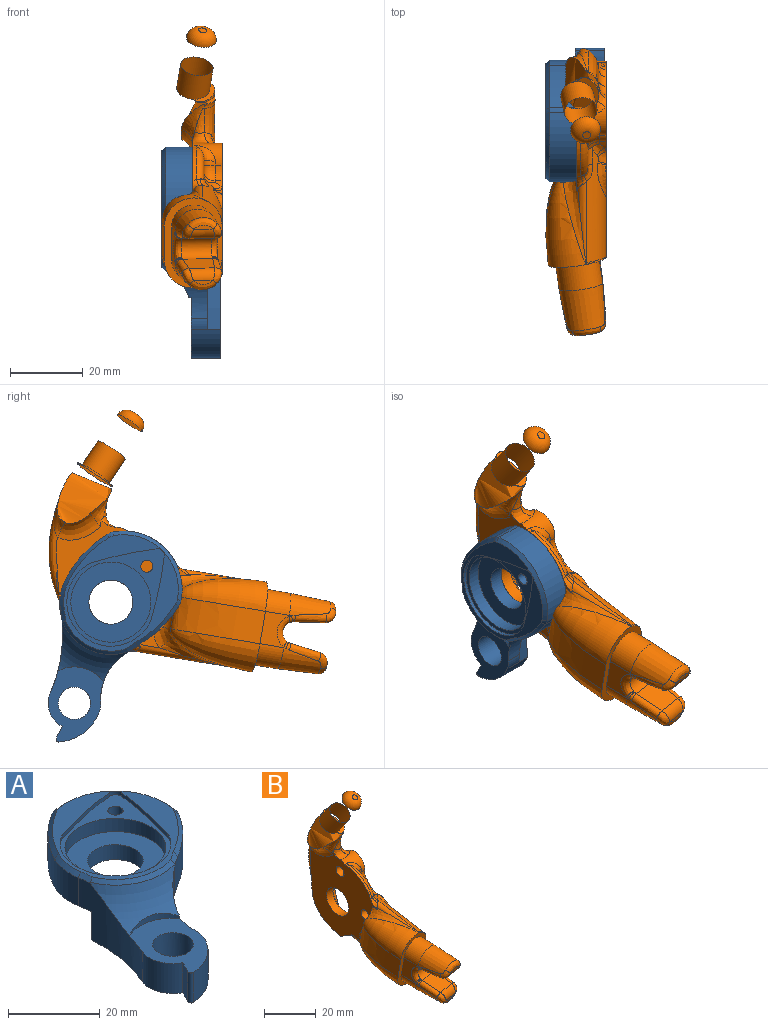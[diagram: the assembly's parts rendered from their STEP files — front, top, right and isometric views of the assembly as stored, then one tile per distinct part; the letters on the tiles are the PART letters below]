
ASSEMBLY  parts=2 mates=1
PART A: 46 faces, bbox 45.5x58x20.8 mm
  f0: cylinder r=15mm len=13.08mm, axis (0,0,-1), area 89.6mm2, adj f3,f6,f18,f19,f21,f31,f42,f44
  f1: cylinder r=40mm len=22.59mm, axis (0,0,-1), area 218.8mm2, adj f3,f6,f7,f11,f12,f21,f31,f40
  f2: cylinder r=4.45mm len=8.9mm, axis (0,0,-1), area 223.7mm2, adj f7,f31
  f3: torus R=25.75mm, axis (0,0,-1), area 148.1mm2, adj f0,f1,f18,f34,f40,f42,f43
  f4: cylinder r=6.06mm len=12.13mm, axis (0,0,-1), area 152.4mm2, adj f6,f33
  f5: cylinder r=1.65mm len=7.5mm, axis (0,0,-1), area 77.8mm2, adj f6,f30
  f6: plane 35.24x33.45mm, normal (0,0,-1), area 708.6mm2, adj f0,f1,f4,f5,f12,f13,f14,f15
  f7: plane 32.44x13.88mm, normal (0,0,-1), area 216.4mm2, adj f1,f2,f8,f9,f10,f11,f19,f21
  f8: cylinder r=12.7mm len=10.93mm, axis (0,0,-1), area 113.9mm2, adj f7,f9,f19,f31
  f9: cylinder r=0.75mm len=8mm, axis (0,0,-1), area 12.7mm2, adj f7,f8,f10,f31
  f10: plane 8x3.14mm, normal (-0.89,0.46,0), area 28.3mm2, adj f7,f9,f11,f31
  f11: cylinder r=7.2mm len=9.28mm, axis (0,0,-1), area 86.6mm2, adj f1,f7,f10,f31
  f12: cylinder r=13.95mm len=8.84mm, axis (0,0,-1), area 68.4mm2, adj f1,f6,f13,f41
  f13: cylinder r=31.7mm len=12.1mm, axis (0,0,-1), area 126.2mm2, adj f6,f12,f14,f39
  f14: cylinder r=4.26mm len=7.5mm, axis (0,0,-1), area 11.6mm2, adj f6,f13,f15,f38
  f15: cylinder r=16mm len=18.98mm, axis (0,0,-1), area 233.5mm2, adj f6,f14,f16,f37
  f16: cylinder r=4.26mm len=7.5mm, axis (0,0,-1), area 11.6mm2, adj f6,f15,f17,f36
  f17: cylinder r=31.7mm len=11.35mm, axis (0,0,-1), area 119.7mm2, adj f6,f16,f18,f35
  f18: plane 7.62x3.72mm, normal (0.56,-0.83,0), area 32.2mm2, adj f0,f3,f6,f17,f34
  f19: cylinder r=7.2mm len=8mm, axis (0,0,-1), area 13.9mm2, adj f0,f7,f8,f31,f44,f45
  f20: plane 31.95x31.45mm, normal (0,0,1), area 218.2mm2, adj f26,f27,f28,f29,f34,f35,f36,f37
  f21: cylinder r=19.3mm len=15.31mm, axis (0,0,-1), area 111.5mm2, adj f0,f1,f6,f7,f44,f45
  f22: cylinder r=2mm len=4.5mm, axis (0,0,-1), area 56.5mm2, adj f6,f23
  f23: plane 4x4mm, normal (0,0,-1), area 12.6mm2, adj f22
  f24: cylinder r=2mm len=4.5mm, axis (0,0,-1), area 56.5mm2, adj f6,f25
  f25: plane 4x4mm, normal (0,0,-1), area 12.6mm2, adj f24
  f26: cylinder r=12.1mm len=22.96mm, axis (0,0,1), area 45.5mm2, adj f20,f27,f29,f30
  f27: cylinder r=101.52mm len=18.42mm, axis (0,0,1), area 18.9mm2, adj f20,f26,f28,f30
  f28: cylinder r=1.78mm len=1.99mm, axis (0,0,1), area 3.2mm2, adj f20,f27,f29,f30,f37
  f29: cylinder r=101.6mm len=17.98mm, axis (0,0,1), area 18.4mm2, adj f20,f26,f28,f30
  f30: plane 26.75x26.74mm, normal (0,0,1), area 142.4mm2, adj f5,f26,f27,f28,f29,f32
  f31: plane 20.62x15.22mm, normal (0,0,1), area 164.7mm2, adj f0,f1,f2,f8,f9,f10,f11,f19
  f32: cylinder r=11mm len=22mm, axis (0,0,1), area 241.9mm2, adj f30,f33
  f33: plane 22x22mm, normal (0,0,1), area 264.7mm2, adj f4,f32
  f34: plane 3.03x2.54mm, normal (0.4,-0.58,0.71), area 4.4mm2, adj f3,f18,f20,f35,f43
  f35: cone r=30.7mm half-angle=45deg, axis (0,0,-1), area 22.2mm2, adj f17,f20,f34,f36
  f36: cone r=3.26mm half-angle=45deg, axis (0,0,-1), area 1.9mm2, adj f16,f20,f35,f37
  f37: cone r=15mm half-angle=45deg, axis (0,0,-1), area 42.6mm2, adj f15,f20,f28,f36,f38
  f38: cone r=3.26mm half-angle=45deg, axis (0,0,-1), area 1.9mm2, adj f14,f20,f37,f39
  f39: cone r=30.7mm half-angle=45deg, axis (0,0,-1), area 23.4mm2, adj f13,f20,f38,f41
  f40: cone r=41mm half-angle=45deg, axis (0,0,1), area 4.5mm2, adj f1,f3,f20,f41,f43
  f41: cone r=12.95mm half-angle=45deg, axis (0,0,-1), area 12.4mm2, adj f12,f20,f39,f40
  f42: cylinder r=10mm len=12.52mm, axis (0,0,-1), area 15.4mm2, adj f0,f1,f3,f31
  f43: cone r=14.35mm half-angle=45deg, axis (0,0,-1), area 26.6mm2, adj f3,f20,f34,f40
  f44: plane 17.28x8.22mm, normal (0,0,-1), area 41.2mm2, adj f0,f19,f21,f45
  f45: cylinder r=60mm len=17.28mm, axis (0,0,-1), area 61.5mm2, adj f7,f19,f21,f44
PART B: 155 faces, bbox 20.8x82.2x73.4 mm
  f0: cylinder r=12.5mm len=6.57mm, axis (1,0,0), area 12.3mm2, adj f1,f152,f153,f154
  f1: bspline ~8.61x5.45mm, area 19mm2, adj f0,f2,f151,f152
  f2: bspline ~5.83x3.21mm, area 6.3mm2, adj f1,f3,f151,f154
  f3: bspline ~5.94x4.58mm, area 11.8mm2, adj f2,f4,f151,f154
  f4: torus R=16.27mm, axis (1,0,0), area 12.9mm2, adj f3,f5,f150,f154
  f5: torus R=2.08mm, axis (-1,0,0), area 13.6mm2, adj f4,f6,f150,f154
  f6: torus R=8.42mm, axis (1,0,0), area 9.9mm2, adj f5,f7,f150,f154
  f7: bspline ~5.11x5.08mm, area 15.8mm2, adj f6,f8,f149,f154
  f8: bspline ~6.78x6.46mm, area 16.2mm2, adj f7,f9,f148,f149
  f9: bspline ~8.16x4.84mm, area 20.1mm2, adj f8,f10,f146,f147,f148
  f10: plane 39.01x37.95mm, normal (-1,0,0), area 818.2mm2, adj f9,f11,f13,f98,f100,f107,f125,f126
  f11: cylinder r=2.2mm len=5.72mm, axis (1,0,0), area 79.1mm2, adj f10,f12
  f12: cone r=2.2mm half-angle=45deg, axis (1,0,0), area 67.7mm2, adj f11,f154
  f13: cylinder r=6.06mm len=12.13mm, axis (1,0,0), area 133.3mm2, adj f10,f14
  f14: cone r=7.06mm half-angle=45deg, axis (1,0,0), area 58.3mm2, adj f13,f15
  f15: plane 28.47x25.56mm, normal (1,0,0), area 304.6mm2, adj f14,f16,f18,f91,f92,f93,f94,f95
  f16: cylinder r=3.12mm len=2.5mm, axis (1,0,0), area 6.1mm2, adj f15,f17,f18,f140
  f17: bspline ~2.97x2.71mm, area 3.7mm2, adj f16,f136,f139,f140
  f18: plane 18.37x6.1mm, normal (0,0.17,-0.99), area 51.5mm2, adj f15,f16,f19,f89,f90,f91,f136,f154
  f19: bspline ~4.5x3.66mm, area 1.2mm2, adj f18,f20,f89,f135,f136
  f20: cylinder r=2mm len=12.79mm, axis (0,-0.99,-0.17), area 9mm2, adj f19,f21,f135
  f21: cylinder r=8mm len=15.82mm, axis (0,-0.99,-0.17), area 136.6mm2, adj f20,f22,f23,f87,f88,f89,f154
  f22: bspline ~4.09x3.32mm, area 10.9mm2, adj f21,f88,f89,f90
  f23: bspline ~9.23x6.3mm, area 4.3mm2, adj f21,f24,f86,f135,f154
  f24: plane 24.88x16.08mm, normal (0.14,-0.98,-0.16), area 124.1mm2, adj f23,f25,f27,f28,f49,f83,f84,f85
  f25: extruded ~25.96x12.97mm, area 228.4mm2, adj f24,f26,f27,f86,f131,f132,f133
  f26: cylinder r=5mm len=4.28mm, axis (0,0.17,-0.99), area 7.7mm2, adj f25,f133,f134
  f27: revolved ~23.83x13.45mm, area 248.4mm2, adj f24,f25,f28,f130,f131
  f28: bspline ~9.07x6.3mm, area 4.3mm2, adj f24,f27,f29,f130,f154
  f29: cylinder r=8mm len=32.07mm, axis (0,0.99,0.17), area 213.6mm2, adj f28,f30,f31,f32,f34,f45,f46,f47
  f30: bspline ~3.31x2.25mm, area 6.1mm2, adj f29,f31,f48,f154
  f31: bspline ~2.25x1.01mm, area 1.1mm2, adj f29,f30,f32,f154
  f32: bspline ~9.23x7.18mm, area 22.5mm2, adj f29,f31,f33,f154
  f33: cylinder r=5.5mm len=2.12mm, axis (1,0,0), area 0mm2, adj f32,f154
  f34: cylinder r=2mm len=22.47mm, axis (0,0.99,0.17), area 32mm2, adj f29,f35,f128,f130
  f35: bspline ~3.01x2.42mm, area 3.1mm2, adj f34,f36,f45,f128
  f36: torus R=14.05mm, axis (1,0,0), area 38.7mm2, adj f35,f37,f44,f45,f127
  f37: bspline ~6.23x5.24mm, area 19.2mm2, adj f36,f38,f126,f148
  f38: torus R=8.62mm, axis (1,0,0), area 6.7mm2, adj f37,f39,f44,f148
  f39: torus R=1.88mm, axis (1,0,0), area 18.3mm2, adj f38,f40,f43,f44
  f40: torus R=16.47mm, axis (1,0,0), area 5.2mm2, adj f39,f41,f44,f46,f47
  f41: cylinder r=13.35mm len=1.88mm, axis (1,0,0), area 3.1mm2, adj f40,f42,f43,f47,f154
  f42: cylinder r=5mm len=0.99mm, axis (-1,0,0), area 0.2mm2, adj f41,f48,f154
  f43: cylinder r=5mm len=4.29mm, axis (1,0,0), area 9.1mm2, adj f39,f41,f148,f154
  f44: plane 5.2x4.56mm, normal (1,0,0), area 10.8mm2, adj f36,f38,f39,f40,f46
  f45: bspline ~6.77x3.55mm, area 10.4mm2, adj f29,f35,f36,f46
  f46: cylinder r=3.12mm len=5.08mm, axis (0,0.99,0.17), area 13.4mm2, adj f29,f40,f44,f45,f47
  f47: bspline ~3.72x3.62mm, area 7.2mm2, adj f29,f40,f41,f46,f48
  f48: bspline ~3.61x3.59mm, area 2.7mm2, adj f29,f30,f42,f47
  f49: plane 10.04x8.34mm, normal (0.99,0.14,0.02), area 47.1mm2, adj f24,f50,f81,f82,f83,f85
  f50: plane 0.5x0.32mm, normal (0.99,0.1,0.02), area 0.1mm2, adj f49,f51,f80
  f51: cone r=6mm half-angle=2.2deg, axis (-0.14,0.98,0.16), area 176.9mm2, adj f50,f52,f73,f74,f75,f76,f77,f78
  f52: bspline ~4.56x3.76mm, area 14.6mm2, adj f51,f53,f73,f79
  f53: cylinder r=3mm len=7.35mm, axis (-0.99,-0.14,-0.02), area 26.9mm2, adj f52,f54,f55,f74
  f54: plane 5.36x1.22mm, normal (0.14,-0.98,-0.16), area 4.2mm2, adj f53,f73
  f55: plane 9.26x8.79mm, normal (0.02,-0.29,0.96), area 66.9mm2, adj f53,f56,f75,f79
  f56: cylinder r=3.01mm len=8.68mm, axis (-0.99,-0.14,-0.02), area 72.4mm2, adj f55,f57,f58,f59,f69,f70,f71,f72
  f57: bspline ~2.59x2.49mm, area 1.5mm2, adj f56,f72,f77,f78
  f58: bspline ~2.71x2.45mm, area 1.6mm2, adj f56,f59,f81,f82
  f59: bspline ~1.97x1.92mm, area 2.2mm2, adj f56,f58,f60,f68
  f60: cone r=5.5mm half-angle=2.2deg, axis (-0.14,0.98,0.16), area 177.4mm2, adj f59,f61,f64,f65,f66,f67,f68,f70
  f61: bspline ~4.06x3.34mm, area 14.5mm2, adj f60,f62,f64,f68
  f62: cylinder r=3mm len=7.35mm, axis (0.99,0.14,0.02), area 26.8mm2, adj f61,f63,f65,f69
  f63: plane 5.38x1.23mm, normal (0.14,-0.98,-0.16), area 4.3mm2, adj f62,f64
  f64: bspline ~8.13x3.29mm, area 22.5mm2, adj f60,f61,f63,f65
  f65: bspline ~4.08x3.74mm, area 14.5mm2, adj f60,f62,f64,f66
  f66: bspline ~9.15x3.66mm, area 29.9mm2, adj f60,f65,f69,f70
  f67: plane 0.7x0.29mm, normal (-0.98,-0.17,-0.03), area 0.1mm2, adj f60,f71,f84
  f68: bspline ~8.88x3.24mm, area 29.9mm2, adj f59,f60,f61,f69
  f69: plane 9.68x8.8mm, normal (0.02,0.03,-1), area 67.3mm2, adj f56,f62,f66,f68
  f70: bspline ~1.98x1.92mm, area 2.2mm2, adj f56,f60,f66,f71
  f71: bspline ~1.97x1.83mm, area 1.5mm2, adj f56,f67,f70,f72
  f72: bspline ~8.42x3.68mm, area 23.1mm2, adj f56,f57,f71,f84
  f73: bspline ~8.09x2.93mm, area 22.4mm2, adj f51,f52,f54,f74
  f74: bspline ~4.54x3.13mm, area 14.6mm2, adj f51,f53,f73,f75
  f75: bspline ~9.01x4.92mm, area 29.9mm2, adj f51,f55,f74,f76
  f76: bspline ~2.13x1.96mm, area 2.7mm2, adj f51,f56,f75,f80
  f77: plane 0.5x0.32mm, normal (-0.98,-0.17,-0.03), area 0.1mm2, adj f51,f57,f84
  f78: bspline ~2.2x2.02mm, area 2.7mm2, adj f51,f56,f57,f79
  f79: bspline ~8.95x4.96mm, area 29.9mm2, adj f51,f52,f55,f78
  f80: bspline ~2.7x2.51mm, area 1.5mm2, adj f50,f56,f76,f81
  f81: bspline ~8.42x4.1mm, area 23.1mm2, adj f49,f56,f58,f80
  f82: plane 0.7x0.29mm, normal (0.99,0.1,0.02), area 0.1mm2, adj f49,f58,f60
  f83: cylinder r=6mm len=12.86mm, axis (-0.14,0.98,0.16), area 131.9mm2, adj f24,f49,f60,f84
  f84: plane 10.04x8.34mm, normal (-0.99,-0.14,-0.02), area 47.1mm2, adj f24,f67,f72,f77,f83,f85
  f85: cylinder r=6mm len=12.86mm, axis (-0.14,0.98,0.16), area 131.9mm2, adj f24,f49,f51,f84
  f86: revolved ~24.58x13.44mm, area 251.5mm2, adj f23,f24,f25,f134,f135
  f87: bspline ~1.24x1.23mm, area 0.2mm2, adj f21,f88,f154
  f88: bspline ~4.08x3.04mm, area 3.8mm2, adj f21,f22,f87,f154
  f89: bspline ~2.93x2.25mm, area 4.5mm2, adj f18,f19,f21,f22
  f90: plane 4.03x3.18mm, normal (0.64,-0.61,-0.46), area 7.7mm2, adj f18,f22,f154
  f91: cylinder r=5mm len=3.93mm, axis (1,0,0), area 19.1mm2, adj f15,f18,f92,f154
  f92: plane 15.14x4.92mm, normal (0,0.95,-0.31), area 55.7mm2, adj f15,f91,f93,f154
  f93: cylinder r=10.05mm len=19.61mm, axis (1,0,0), area 111.2mm2, adj f15,f92,f94,f95,f96,f154
  f94: plane 1.41x0.79mm, normal (0,-0.88,0.48), area 0.2mm2, adj f15,f93,f95
  f95: bspline ~8.96x8.81mm, area 0.5mm2, adj f15,f93,f94,f96
  f96: plane 3.9x3.57mm, normal (0,-0.95,0.31), area 13.5mm2, adj f15,f93,f95,f97,f154
  f97: plane 5.95x3.5mm, normal (0,-0.94,0.34), area 22.1mm2, adj f15,f96,f141,f154
  f98: cylinder r=2.2mm len=5.72mm, axis (1,0,0), area 79.1mm2, adj f10,f99
  f99: cone r=2.2mm half-angle=45deg, axis (1,0,0), area 67.7mm2, adj f98,f154
  f100: bspline ~9.75x4.8mm, area 6.4mm2, adj f10,f101,f107,f145
  f101: bspline ~3.53x2.52mm, area 2.2mm2, adj f100,f102,f106,f107
  f102: sphere r=3.12mm, area 1.5mm2, adj f101,f103,f105
  f103: bspline ~2.88x2.1mm, area 0.6mm2, adj f102,f104,f107,f143
  f104: sphere r=3.12mm, area 1.2mm2, adj f103,f152,f153
  f105: bspline ~3.84x3.76mm, area 3.7mm2, adj f102,f106,f143,f144
  f106: torus R=12.12mm, axis (1,0,0), area 2mm2, adj f101,f105,f145
  f107: bspline ~41.57x9.9mm, area 98.5mm2, adj f10,f100,f101,f103,f108,f151,f152
  f108: bspline ~17.59x6.23mm, area 38.2mm2, adj f107,f109,f124,f125
  f109: revolved ~17.35x15.85mm, area 187.7mm2, adj f108,f110,f122,f123,f124,f125,f147
  f110: plane 13.2x11.17mm, normal (0.13,-0.55,0.82), area 44.2mm2, adj f109,f111,f113,f114,f115,f116,f120,f121
  f111: plane 0.73x0.46mm, normal (1,0,0), area 0mm2, adj f110,f112,f113,f121
  f112: plane 9.81x6.64mm, normal (0,-0.56,0.83), area 23.9mm2, adj f111,f113,f114,f116,f120,f121
  f113: bspline ~7.01x6mm, area 4mm2, adj f110,f111,f112,f114
  f114: bspline ~3.57x3.11mm, area 0.7mm2, adj f110,f112,f113,f115
  f115: cylinder r=4.5mm len=0.02mm, axis (-0.13,0.55,-0.82), area 0mm2, adj f110,f114,f116
  f116: cylinder r=4.5mm len=11.92mm, axis (-0.13,0.55,-0.82), area 220.7mm2, adj f110,f112,f115,f117,f120
  f117: cone r=4mm half-angle=2.4deg, axis (-0.13,0.55,-0.82), area 247.3mm2, adj f116,f118
  f118: torus R=1.12mm, axis (0.13,-0.55,0.82), area 86.5mm2, adj f117,f119
  f119: plane 2.22x1.87mm, normal (0.13,-0.55,0.82), area 4mm2, adj f118
  f120: bspline ~3.82x3.11mm, area 0.7mm2, adj f110,f112,f116,f121
  f121: bspline ~6.5x6mm, area 4mm2, adj f110,f111,f112,f120
  f122: bspline ~6.81x3.61mm, area 8mm2, adj f109,f123,f147,f149
  f123: bspline ~1.59x1.32mm, area 0.4mm2, adj f109,f122,f124,f150
  f124: bspline ~6.33x4.77mm, area 4.5mm2, adj f108,f109,f123,f151
  f125: bspline ~15.2x9.34mm, area 58.6mm2, adj f10,f108,f109,f147
  f126: cylinder r=3.12mm len=1.2mm, axis (1,0,0), area 1.3mm2, adj f10,f37,f127,f148
  f127: cylinder r=16.05mm len=12.86mm, axis (-1,0,0), area 16.4mm2, adj f10,f36,f126,f128
  f128: bspline ~4.94x4.15mm, area 5.6mm2, adj f10,f34,f35,f127,f129
  f129: bspline ~3.2x3.16mm, area 0.2mm2, adj f10,f128,f130
  f130: bspline ~25.29x6.42mm, area 61.3mm2, adj f10,f27,f28,f34,f129,f131
  f131: cylinder r=16.05mm len=7.09mm, axis (1,0,0), area 20.9mm2, adj f10,f25,f27,f130,f132
  f132: cylinder r=4.3mm len=5.45mm, axis (1,0,0), area 8.1mm2, adj f10,f25,f131,f133
  f133: cylinder r=31.75mm len=7.93mm, axis (1,0,0), area 23.1mm2, adj f10,f25,f26,f132,f134
  f134: bspline ~8.94x6.71mm, area 24.2mm2, adj f10,f26,f86,f133,f135
  f135: bspline ~25.62x9.6mm, area 66.3mm2, adj f10,f19,f20,f23,f86,f134,f136
  f136: cylinder r=2mm len=22.24mm, axis (0,-0.99,-0.17), area 48.6mm2, adj f10,f17,f18,f19,f135,f137,f138,f139
  f137: cylinder r=31.75mm len=0.62mm, axis (-1,0,0), area 0mm2, adj f10,f136,f138
  f138: extruded ~0.83x0.12mm, area 0mm2, adj f10,f136,f137,f139
  f139: bspline ~4.12x2.02mm, area 3mm2, adj f10,f17,f136,f138
  f140: extruded ~4.5x2.5mm, area 11.7mm2, adj f10,f15,f16,f17,f141
  f141: cylinder r=19.03mm len=8.85mm, axis (1,0,0), area 44.1mm2, adj f10,f15,f97,f140,f142,f154
  f142: cylinder r=14.23mm len=8mm, axis (1,0,0), area 86.1mm2, adj f10,f141,f143,f154
  f143: extruded ~8x2mm, area 12.5mm2, adj f10,f103,f105,f142,f144,f153,f154
  f144: cylinder r=3.12mm len=1mm, axis (1,0,0), area 0.6mm2, adj f10,f105,f143,f145
  f145: cylinder r=14.12mm len=3.95mm, axis (-1,0,0), area 3.7mm2, adj f10,f100,f106,f144
  f146: bspline ~9.09x4.94mm, area 9.9mm2, adj f9,f147,f149
  f147: bspline ~11.47x7.16mm, area 34.9mm2, adj f9,f10,f109,f122,f125,f146
  f148: cylinder r=5.5mm len=8mm, axis (1,0,0), area 44.6mm2, adj f8,f9,f10,f37,f38,f43,f126,f154
  f149: bspline ~15.88x7.67mm, area 57.2mm2, adj f7,f8,f122,f146,f150
  f150: plane 19.91x5.35mm, normal (1,0,0), area 52mm2, adj f4,f5,f6,f123,f149,f151
  f151: bspline ~39.33x12.84mm, area 177.5mm2, adj f1,f2,f3,f107,f124,f150
  f152: bspline ~3.32x2.79mm, area 2mm2, adj f0,f1,f104,f107
  f153: cylinder r=3.12mm len=3.85mm, axis (1,0,0), area 6.3mm2, adj f0,f104,f143,f154
  f154: plane 54.29x36.6mm, normal (1,0,0), area 459.2mm2, adj f0,f2,f3,f4,f5,f6,f7,f12
PLACE A rot(axis=(0.58,-0.58,-0.58),120deg) t=(-5.32,90.51,107.71)mm
PLACE B rot(axis=(-1,0,0),0deg) t=(-4.82,-369.49,107.71)mm
MATE fastened B.f4 <-> A.f3  axis (-1,0,0) through (-12.82,90.51,107.71)mm
